# Revit family: IS_StradaII_T3724_BIM_NL
name_source: partatom
category: Plumbing Fixtures
revit_build: Autodesk Revit 2017 (Build: 20171027_0315(x64)
units: mm (PartAtom-declared; Revit-internal decimal feet)

## family parameters
Always vertical = No
Cut with Voids When Loaded = No
OmniClass Number = 23.45.05.14.14
OmniClass Title = Sinks/Lavatories
Part Type = Normal
Room Calculation Point = No
Round Connector Dimension = Use Diameter
Shared = No
Work Plane-Based = No

## types (2) — shared parameters
AssetType = Fixed
BIMObjectName = ISI_IdealStandard_Washhandbasin_StradaII_T3002
BOSUseNativeGeometries = 1
Brand = Ideal Standard
CurrencyUnit = €
CurrentRevision = 1
Edition number = 1
IfcExportAs = IfcSanitaryTerminalType
IfcExportType = WASHHANDBASIN
InstallationDate = 1900-12-31T23:59:59
Manufacturer name = Ideal Standard
NBS Reference Code = 45-35-70/369
NBS Reference Description = Wall hung wash basins
NominalDepth = 428 mm  [stored 1.4042 ft]
NominalHeight = 178 mm
NominalLength = 428 mm  [stored 1.4042 ft]
NominalWidth = 1000 mm
Product Guid = ef8327f4-e8e8-45e9-a155-51ded0bb0605
Product data url = https://bimobject.com
Product family = Sanitary
Product group = Washbasins
QR code = http://bimobject.com
ReplacementCost = 0
Size = 178 x 428 x 1000mm
Space = Internal
Uniclass 2.0 Code = Pr_40_20_96_96
Uniclass 2.0 Description = Wall hung wash basins
Uniclass 2015 Code = Pr_40_20_96_96
Uniclass 2015 Name = Wall hung wash basins
Uniclass2015Code = Pr_40_20_96_96
Uniclass2015Title = Wall hung wash basins
Uniclass2015Version = Products v1.1
Version = 1
zero-valued in all types: Cost, Nominal height, Nominal width, Weight Net (Kg)

## per-type parameters (varying)
- T372401 - STRADA II WASTAFEL 100CM MET 2 KRAANGATEN METOVERLOOP GESLEPEN ONDERZIJDE: Accessories=www.idealstandardnederland.nl; BarCode=8014140455684; Brand url=www.idealstandardnederland.nl; Category=Sanitair; Color=Wit; ConnectionType=Sanitair; Description=STRADA II WASTAFEL 100CM MET 2 KRAANGATEN METOVERLOOP GESLEPEN ONDERZIJDE; DrainSize=46 mm  [stored 0.150919 ft]; DurationUnit=jaar; EAN code=https://8014140455684; ExpectedLife=25; Features=Wastafel 1000 mm van keramiek. Geslepen onderzijde. 2 kraangaten links en rechts doorgestoken. Met overloop. Met keramische afvoerafdekking. Bevestiging met 4 schroeven M10 x 140 mm (2x K710767). Exclusief bevestigingsmateriaal.; Finish=Wit; GrossWeight=24 kg; Installation instructions=www.idealstandardnederland.nl; InstallationInstructions=www.idealstandardnederland.nl; MainColor=Wit; Manufacturer=www.idealstandardnederland.nl; ManufacturerURL=www.idealstandardnederland.nl; Material=Keramiek; Material main=Keramiek; Model=T372401; ModelNumber=T372401; ModelReference=STRADA II WASTAFEL 100CM MET 2 KRAANGATEN METOVERLOOP GESLEPEN ONDERZIJDE; Name=ISI_IdealStandard_Washhandbasin_StradaII_T3724; NettWeight=22 kg; Product SKU=T3724; Product name=STRADA II WASTAFEL 100CM MET 2 KRAANGATEN METOVERLOOP GESLEPEN ONDERZIJDE; Product url=www.idealstandardnederland.nl; ProductInformation=www.idealstandardnederland.nl; Shape=Gesculptuurd; SpareParts=www.idealstandardnederland.nl; Technical description=www.idealstandardnederland.nl; URL=www.idealstandardnederland.nl; VolumeUnits=liter; WarrantyDurationUnit=jaar; WashHandBasinMounting=Wandhangend; WashHandBasinType=Wastafel
- T3002MA - STRADA II BASIN 100 WHT IP 1TH WHG: Accessories=http://www.idealstandard.de; BarCode=8014140450573; Brand url=http://www.idealstandard.de; Category=Sanitary; Color=WHITE; ConnectionType=Plumbing; Date of publishing=43172; Description=STRADA II BASIN 100 WHT IP 1TH WHG; DrainSize=0 mm  [stored 0 ft]; DurationUnit=year; EAN code=https://8014140450573; Features=BASIN 100 WHT IP 1TH WHG; Finish=WHITE; GrossWeight=24; Installation instructions=http://www.idealstandard.de; InstallationInstructions=http://www.idealstandard.de; MainColor=WHITE; Manufacturer=http://www.idealstandard.de; ManufacturerURL=http://www.idealstandard.de; Material=Fire clay; Model=T3002MA; ModelNumber=T3002MA; ModelReference=STRADA II BASIN 100 WHT IP 1TH WHG; Name=ISI_IdealStandard_Washhandbasin_StradaII_T3002; NettWeight=22; Product SKU=T3002; Product name=STRADA II BASIN 100 WHT IP 1TH WHG; Product url=http://www.idealstandard.de; ProductInformation=http://www.idealstandard.de; Shape=Sculptured; SpareParts=http://www.idealstandard.de; Technical description=http://www.idealstandard.de; URL=http://www.idealstandard.de; VolumeUnits=Litre; WarrantyDurationUnit=year; WashHandBasinMounting=Wall hung; WashHandBasinType=Handrinse

note: [stored X ft] marks values corroborated as IEEE doubles in the binary element streams (Revit-internal decimal feet)

## geometry (parser evidence)
native form markers: Sweep x2
no freeform markers — native parametric forms only
